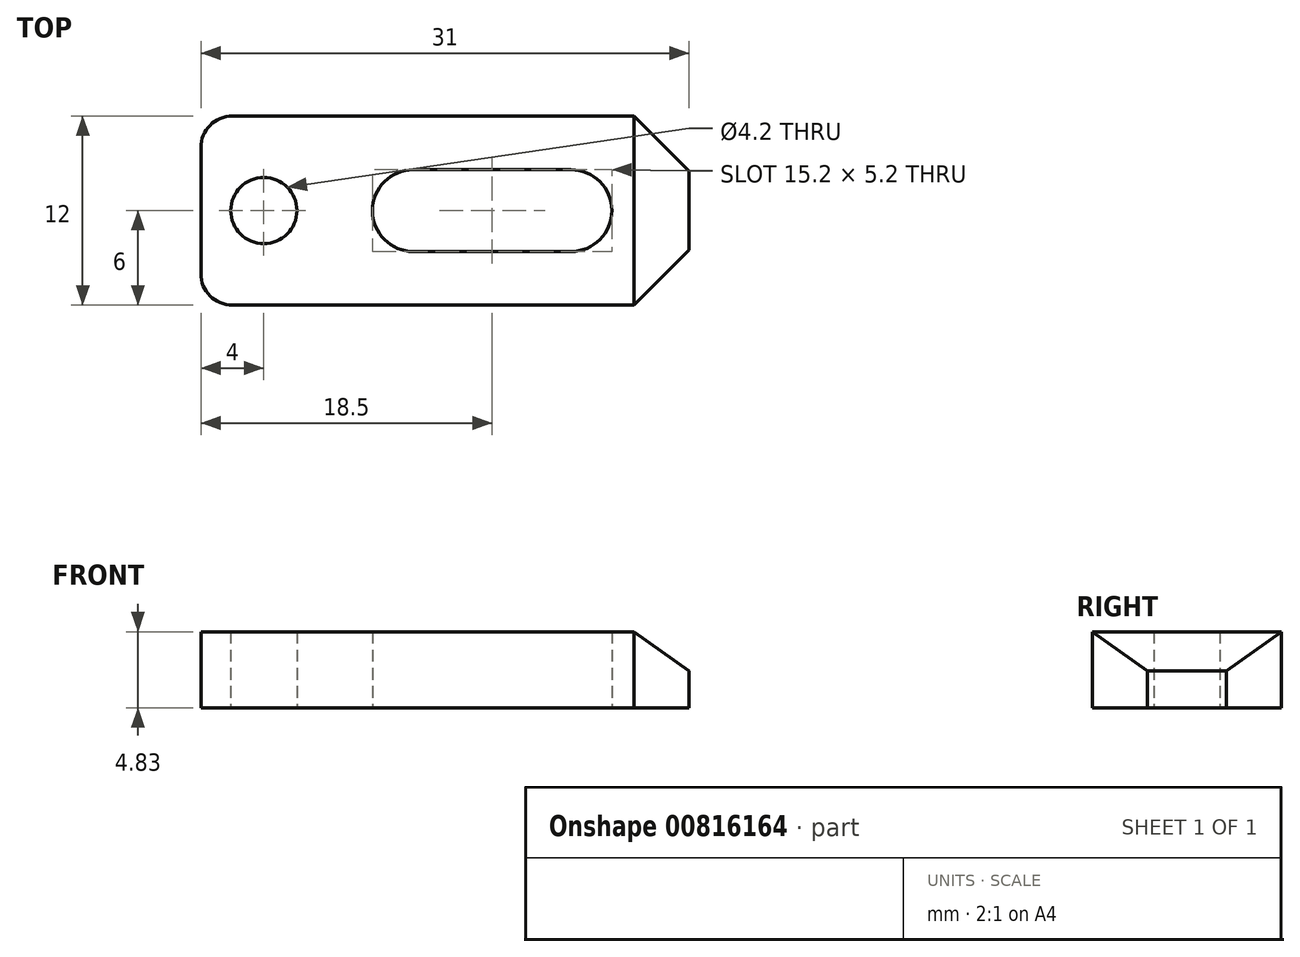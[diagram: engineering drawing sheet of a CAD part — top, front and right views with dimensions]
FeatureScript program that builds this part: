
annotation { "Feature Type Name" : "Feature", "Feature Type Description" : "" }
export const myFeature = defineFeature(function(context is Context, id is Id, definition is map)
    precondition{}
    {
        {
            var Q0;
            Q0=qCreatedBy(makeId("Top.planeOp"),FACE);
            var sketch = newSketch(context, id + "F0", { "sketchPlane" : qUnion([Q0])});
            skLineSegment(sketch, "E0", {"start": v(-5, 0) * mm, "end": v(5, 0) * mm});
            skLineSegment(sketch, "E1.bottom", {"start": v(9, -6) * mm, "end": v(-12.5, -6) * mm});
            skLineSegment(sketch, "E1.top", {"start": v(9, 6) * mm, "end": v(-12.5, 6) * mm});
            skLineSegment(sketch, "E1.left", {"start": v(12.5, -2.5) * mm, "end": v(12.5, 2.5) * mm});
            skPoint(sketch, "E1.middle", {"position": v(0, 0) * mm});
            skArc(sketch, "E2.0.startCap", {"start": v(-5, -2.6) * mm, "mid": v(-7.6, 0) * mm, "end": v(-5, 2.6) * mm});
            skArc(sketch, "E2.0.endCap", {"start": v(5, 2.6) * mm, "mid": v(7.6, 0) * mm, "end": v(5, -2.6) * mm});
            skLineSegment(sketch, "E2.0.left", {"start": v(-5, 2.6) * mm, "end": v(5, 2.6) * mm});
            skLineSegment(sketch, "E2.0.right", {"start": v(-5, -2.6) * mm, "end": v(5, -2.6) * mm});
            skLineSegment(sketch, "E3", {"start": v(9, 6) * mm, "end": v(12.5, 2.5) * mm});
            skLineSegment(sketch, "E4", {"start": v(12.5, -2.5) * mm, "end": v(9, -6) * mm});
            skPoint(sketch, "E5.orphan", {"position": v(12.5, 6) * mm});
            skPoint(sketch, "E6.orphan", {"position": v(12.5, -6) * mm});
            skPoint(sketch, "E7.visualSharp", {"position": v(-12.5, 6) * mm});
            skPoint(sketch, "E8.visualSharp", {"position": v(-12.5, -6) * mm});
            skLineSegment(sketch, "E9.bottom", {"start": v(-12.5, -6) * mm, "end": v(-18.5, -6) * mm});
            skLineSegment(sketch, "E9.top", {"start": v(-12.5, 6) * mm, "end": v(-18.5, 6) * mm});
            skLineSegment(sketch, "E9.right", {"start": v(-18.5, -6) * mm, "end": v(-18.5, 6) * mm});
            skCircle(sketch, "E10", {"center": v(-14.5, 0) * mm, "radius": 2.1 * mm});
            skSolve(sketch);
        }
        {
            var Q0;
            Q0=makeQuery(id+"F0.imprint","IMPRINT",FACE,{"disambiguationData":[TD([[makeQuery(id+"F0.imprint","IMPRINT",EDGE,{"derivedFrom":sQuery(id+"F0.wireOp",EDGE,"E1.bottom")}),-1.0]])]});
            extrude(context, id + "F1", {"entities" : qUnion([Q0]), "depth" : 4.83 * mm, "offsetDistance" : 25 * mm});
        }
        {
            var Q0;
            Q0=makeQuery(id+"F1.opExtrude","CAP_EDGE",EDGE,{"disambiguationData":[OSD([sQuery(id+"F0.wireOp",EDGE,"E1.left")])],"isStart":false});
            chamfer(context, id + "F2", {"entities" : qUnion([Q0]), "chamferType" : ChamferType.TWO_OFFSETS, "width1" : 3.5 * mm, "oppositeDirection" : false, "width2" : 2.5 * mm, "tangentPropagation" : true});
        }
        {
            var Q0;
            Q0=makeQuery(id+"F1.opExtrude","SWEPT_EDGE",EDGE,{"disambiguationData":[OSD([sQuery(id+"F0.wireOp",EDGE,"E9.bottom"),sQuery(id+"F0.wireOp",EDGE,"E9.right")])]});
            fillet(context, id + "F3", {"entities" : qUnion([Q0]), "radius" : 2 * mm, "tangentPropagation" : true, "allowEdgeOverflow" : false});
        }
        {
            var Q0;
            Q0=makeQuery(id+"F1.opExtrude","SWEPT_EDGE",EDGE,{"disambiguationData":[OSD([sQuery(id+"F0.wireOp",EDGE,"E9.top"),sQuery(id+"F0.wireOp",EDGE,"E9.right")])]});
            fillet(context, id + "F4", {"entities" : qUnion([Q0]), "radius" : 2 * mm, "tangentPropagation" : true, "allowEdgeOverflow" : false});
        }
    });
